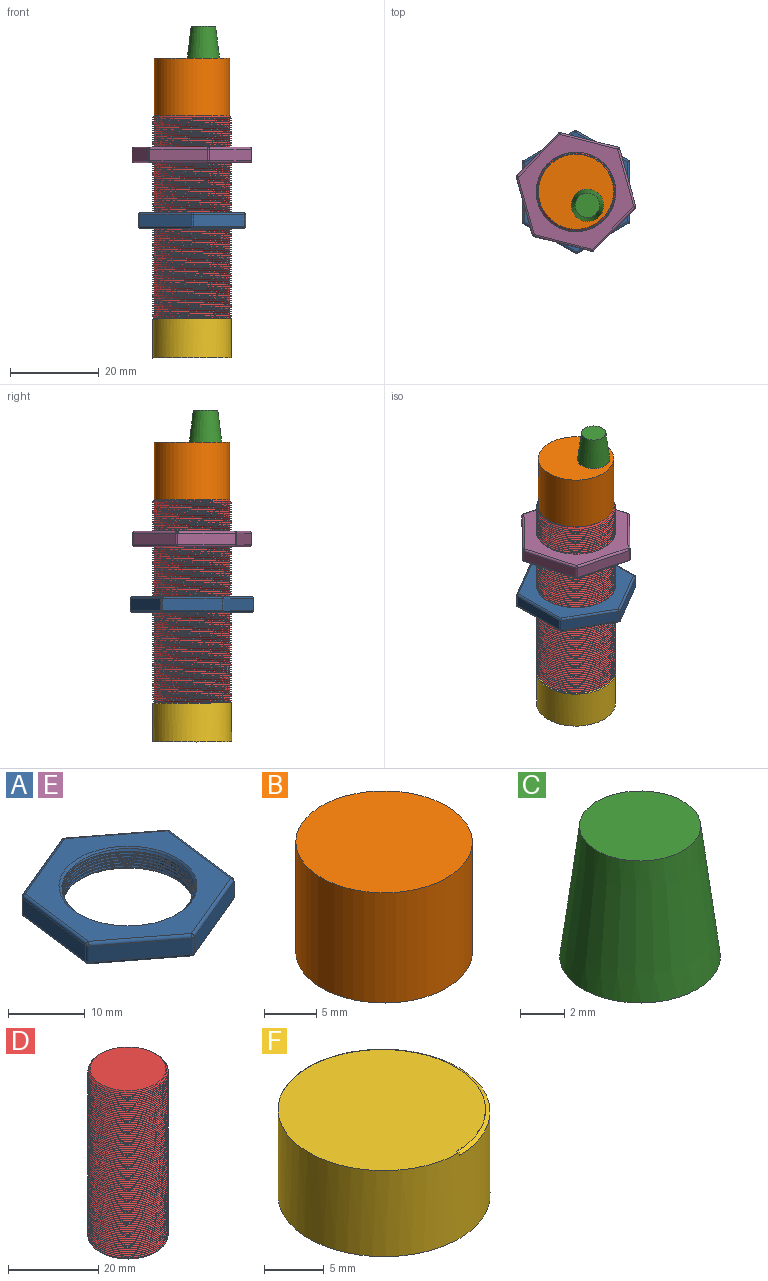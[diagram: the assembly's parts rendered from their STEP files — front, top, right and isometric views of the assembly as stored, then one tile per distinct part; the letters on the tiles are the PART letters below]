
ASSEMBLY  parts=6 mates=5
PART A: 44 faces, bbox 25.7x27.6x3.7 mm
  f0: cone r=8.97mm half-angle=45deg, axis (0,0,-1), area 28.1mm2, adj f7,f10,f41,f42,f43
  f1: cone r=8.47mm half-angle=45deg, axis (0,0,1), area 28.2mm2, adj f7,f9,f41,f42,f43
  f2: plane 10.69x8.17mm, normal (0.61,0.79,0), area 34.8mm2, adj f29,f34,f37,f40
  f3: plane 12.42x5.18mm, normal (-0.38,0.92,0), area 34.8mm2, adj f26,f35,f36,f40
  f4: plane 13.34x2.59mm, normal (-0.99,0.13,0), area 34.8mm2, adj f16,f25,f26,f27
  f5: plane 10.69x8.17mm, normal (-0.61,-0.79,0), area 34.8mm2, adj f11,f15,f16,f17
  f6: plane 12.42x5.18mm, normal (0.38,-0.92,0), area 34.8mm2, adj f11,f14,f18,f19
  f7: cylinder r=8.47mm len=16.95mm, axis (0,0,-1), area 66.1mm2, adj f0,f1,f42,f43
  f8: plane 13.34x2.59mm, normal (0.99,-0.13,0), area 34.8mm2, adj f19,f24,f28,f29
  f9: plane 26.69x24.84mm, normal (0,0,1), area 217.3mm2, adj f1,f14,f15,f24,f25,f34,f35
  f10: plane 26.69x24.84mm, normal (0,0,-1), area 217.3mm2, adj f0,f17,f18,f27,f28,f36,f37
  f11: cylinder r=0.45mm len=2.59mm, axis (0,0,-1), area 1.2mm2, adj f5,f6,f12,f13
  f12: sphere r=0.45mm, area 0.2mm2, adj f11,f14,f15
  f13: sphere r=0.45mm, area 0.1mm2, adj f11,f17,f18
  f14: cylinder r=0.45mm len=12.59mm, axis (-0.92,-0.38,0), area 9.4mm2, adj f6,f9,f12,f20
  f15: cylinder r=0.45mm len=10.96mm, axis (-0.79,0.61,0), area 9.4mm2, adj f5,f9,f12,f21
  f16: cylinder r=0.45mm len=2.59mm, axis (0,0,-1), area 1.2mm2, adj f4,f5,f21,f22
  f17: cylinder r=0.45mm len=10.96mm, axis (0.79,-0.61,0), area 9.4mm2, adj f5,f10,f13,f22
  f18: cylinder r=0.45mm len=12.59mm, axis (0.92,0.38,0), area 9.4mm2, adj f6,f10,f13,f23
  f19: cylinder r=0.45mm len=2.59mm, axis (0,0,-1), area 1.2mm2, adj f6,f8,f20,f23
  f20: sphere r=0.45mm, area 0.2mm2, adj f14,f19,f24
  f21: sphere r=0.45mm, area 0.2mm2, adj f15,f16,f25
  f22: sphere r=0.45mm, area 0.2mm2, adj f16,f17,f27
  f23: sphere r=0.45mm, area 0.2mm2, adj f18,f19,f28
  f24: cylinder r=0.45mm len=13.4mm, axis (-0.13,-0.99,0), area 9.4mm2, adj f8,f9,f20,f30
  f25: cylinder r=0.45mm len=13.4mm, axis (0.13,0.99,0), area 9.4mm2, adj f4,f9,f21,f31
  f26: cylinder r=0.45mm len=2.59mm, axis (0,0,-1), area 1.2mm2, adj f3,f4,f31,f32
  f27: cylinder r=0.45mm len=13.4mm, axis (-0.13,-0.99,0), area 9.4mm2, adj f4,f10,f22,f32
  f28: cylinder r=0.45mm len=13.4mm, axis (0.13,0.99,0), area 9.4mm2, adj f8,f10,f23,f33
  f29: cylinder r=0.45mm len=2.59mm, axis (0,0,-1), area 1.2mm2, adj f2,f8,f30,f33
  f30: sphere r=0.45mm, area 0.2mm2, adj f24,f29,f34
  f31: sphere r=0.45mm, area 0.2mm2, adj f25,f26,f35
  f32: sphere r=0.45mm, area 0.2mm2, adj f26,f27,f36
  f33: sphere r=0.45mm, area 0.1mm2, adj f28,f29,f37
  f34: cylinder r=0.45mm len=10.96mm, axis (0.79,-0.61,0), area 9.4mm2, adj f2,f9,f30,f38
  f35: cylinder r=0.45mm len=12.59mm, axis (0.92,0.38,0), area 9.4mm2, adj f3,f9,f31,f38
  f36: cylinder r=0.45mm len=12.59mm, axis (-0.92,-0.38,0), area 9.4mm2, adj f3,f10,f32,f39
  f37: cylinder r=0.45mm len=10.96mm, axis (-0.79,0.61,0), area 9.4mm2, adj f2,f10,f33,f39
  f38: sphere r=0.45mm, area 0.4mm2, adj f34,f35,f40
  f39: sphere r=0.45mm, area 0.3mm2, adj f36,f37,f40
  f40: cylinder r=0.45mm len=2.59mm, axis (0,0,-1), area 1.2mm2, adj f2,f3,f38,f39
  f41: bspline ~20.28x17.56mm, area 140.5mm2, adj f0,f1,f42,f43
  f42: bspline ~19.76x17.11mm, area 44.2mm2, adj f0,f1,f7,f41
  f43: bspline ~20.28x17.56mm, area 92.2mm2, adj f0,f1,f7,f41
PART B: 3 faces, bbox 17x17x13 mm
  f0: cylinder r=8.47mm len=16.95mm, axis (0,0,-1), area 689.6mm2, adj f1,f2
  f1: plane 16.95x16.95mm, normal (0,0,1), area 225.6mm2, adj f0
  f2: plane 16.95x16.95mm, normal (0,0,-1), area 225.6mm2, adj f0
PART C: 3 faces, bbox 7.3x7.3x7.3 mm
  f0: cone r=3.65mm half-angle=7deg, axis (0,0,-1), area 147mm2, adj f1,f2
  f1: plane 5.51x5.51mm, normal (0,0,1), area 23.8mm2, adj f0
  f2: plane 7.29x7.29mm, normal (0,0,-1), area 41.7mm2, adj f0
PART D: 8 faces, bbox 20.6x17.8x46 mm
  f0: cone r=8.41mm half-angle=45deg, axis (0,0,-1), area 24.3mm2, adj f1,f4,f6,f7
  f1: cone r=8.41mm half-angle=45deg, axis (0,0,-1), area 0.5mm2, adj f0,f3,f7
  f2: cone r=8.91mm half-angle=45deg, axis (0,0,1), area 24.8mm2, adj f3,f5,f6,f7
  f3: cylinder r=8.91mm len=44.78mm, axis (0,0,-1), area 68.7mm2, adj f1,f2,f6,f7
  f4: plane 16.82x16.82mm, normal (0,0,1), area 222.2mm2, adj f0
  f5: plane 16.82x16.82mm, normal (0,0,-1), area 222.2mm2, adj f2
  f6: bspline ~45.81x20.58mm, area 2210.6mm2, adj f0,f2,f3,f7
  f7: bspline ~45.81x20.58mm, area 2224.2mm2, adj f0,f1,f2,f3,f6
PART E: same geometry as A
PART F: 6 faces, bbox 19.6x18.2x9.5 mm
  f0: cylinder r=8.91mm len=17.82mm, axis (0,0,1), area 490.6mm2, adj f1,f2,f3,f5
  f1: plane 18.14x17.92mm, normal (0,0,1), area 242mm2, adj f0,f3,f4,f5
  f2: plane 17.82x17.82mm, normal (0,0,-1), area 249.4mm2, adj f0
  f3: plane 0.39x0.3mm, normal (1,0,0), area 0.1mm2, adj f0,f1,f4,f5
  f4: bspline ~7.72x4.65mm, area 0.5mm2, adj f1,f3,f5
  f5: bspline ~18x17.82mm, area 9mm2, adj f0,f1,f3,f4
PLACE A rot(axis=(0,0,1),67.7deg) t=(-31.69,-6.18,7.99)mm
PLACE B rot(axis=(0,0,1),130.1deg) t=(-31.69,-6.18,-12.4)mm
PLACE C rot(axis=(0,0,1),130.1deg) t=(-32.65,-12.21,-12.4)mm
PLACE D rot(axis=(0,0,1),130.1deg) t=(-31.69,-6.18,-12.4)mm
PLACE E rot(axis=(0,0,1),83.1deg) t=(-31.69,-6.18,22.78)mm
PLACE F rot(axis=(0,0,1),130.1deg) t=(-31.69,-6.18,-12.4)mm
MATE cylindrical E.f0 <-> B.f0  axis (0,0,-1) through (-31.69,-6.18,22.78)mm
MATE fastened D.f0 <-> F.f0  axis (0,0,-1) through (-31.69,-6.18,-12.4)mm
MATE cylindrical A.f0 <-> B.f0  axis (0,0,-1) through (-31.69,-6.18,7.99)mm
MATE fastened C.f0 <-> B.f1  axis (0,0,-1) through (-29.12,-9.24,46.33)mm
MATE fastened B.f0 <-> D.f0  axis (0,0,-1) through (-31.69,-6.18,33.38)mm
